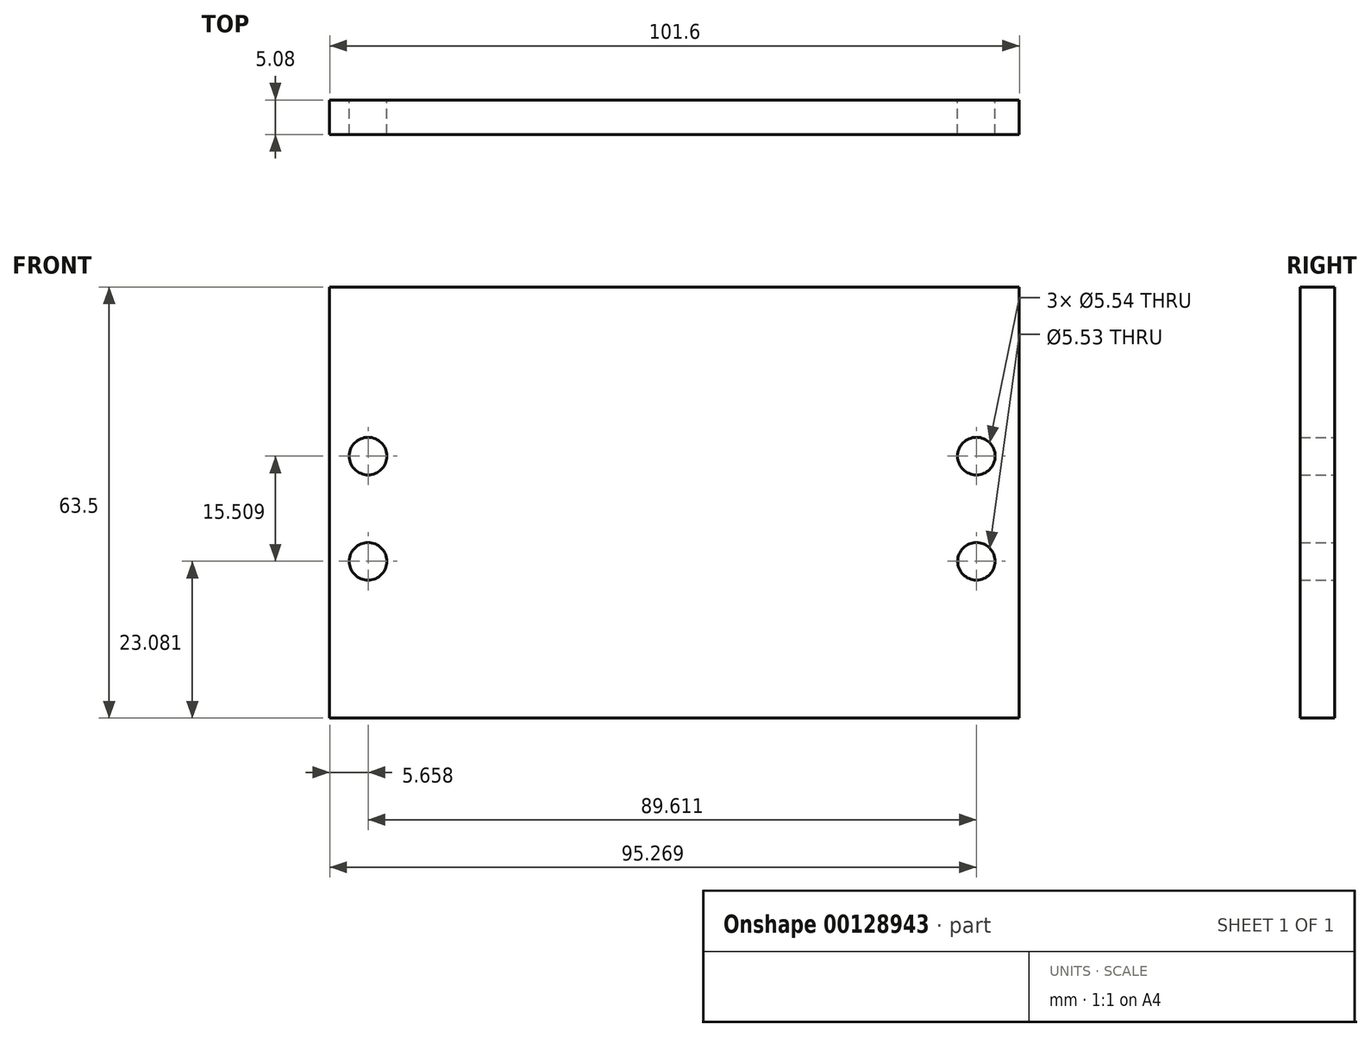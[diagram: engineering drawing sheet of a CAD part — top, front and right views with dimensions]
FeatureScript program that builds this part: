
annotation { "Feature Type Name" : "Feature", "Feature Type Description" : "" }
export const myFeature = defineFeature(function(context is Context, id is Id, definition is map)
    precondition{}
    {
        {
            var Q0;
            Q0=qCreatedBy(makeId("Front.planeOp"),FACE);
            var sketch = newSketch(context, id + "F0", { "sketchPlane" : qUnion([Q0])});
            skLineSegment(sketch, "E0.bottom", {"start": v(-50.51, 33.37) * mm, "end": v(51.09, 33.37) * mm});
            skLineSegment(sketch, "E0.top", {"start": v(-50.51, -30.13) * mm, "end": v(51.09, -30.13) * mm});
            skLineSegment(sketch, "E0.left", {"start": v(-50.51, 33.37) * mm, "end": v(-50.51, -30.13) * mm});
            skLineSegment(sketch, "E0.right", {"start": v(51.09, 33.37) * mm, "end": v(51.09, -30.13) * mm});
            skCircle(sketch, "E1", {"center": v(44.76, -7.05) * mm, "radius": 2.76 * mm});
            skCircle(sketch, "E2", {"center": v(44.76, 8.46) * mm, "radius": 2.77 * mm});
            skCircle(sketch, "E3", {"center": v(-44.85, -7.05) * mm, "radius": 2.77 * mm});
            skCircle(sketch, "E4", {"center": v(-44.85, 8.46) * mm, "radius": 2.77 * mm});
            skLineSegment(sketch, "E5", {"start": v(-44.85, 8.46) * mm, "end": v(-44.85, -7.05) * mm});
            skLineSegment(sketch, "E6", {"start": v(44.76, 8.46) * mm, "end": v(44.76, -7.05) * mm});
            skSolve(sketch);
        }
        {
            var Q0;
            Q0=makeQuery(id+"F0.imprint","IMPRINT",FACE,{"disambiguationData":[TD([[makeQuery(id+"F0.imprint","IMPRINT",EDGE,{"derivedFrom":sQuery(id+"F0.wireOp",EDGE,"E0.bottom")}),-1.0]])]});
            extrude(context, id + "F1", {"entities" : qUnion([Q0]), "depth" : 5.08 * mm});
        }
    });
